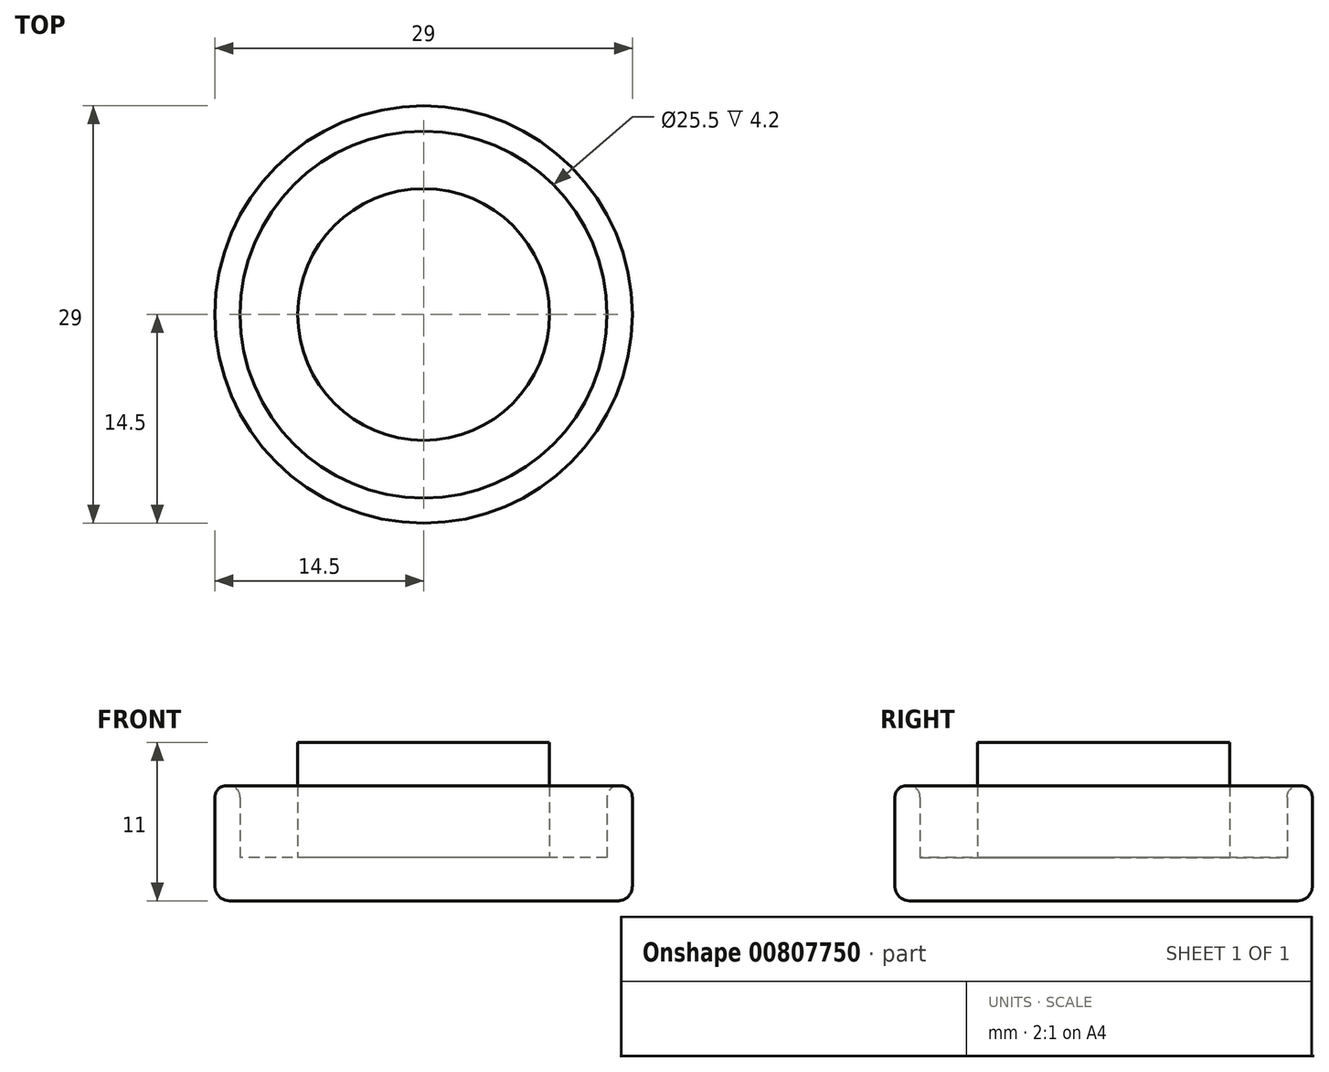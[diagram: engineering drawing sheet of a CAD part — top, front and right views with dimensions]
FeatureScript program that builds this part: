
annotation { "Feature Type Name" : "Feature", "Feature Type Description" : "" }
export const myFeature = defineFeature(function(context is Context, id is Id, definition is map)
    precondition{}
    {
        {
            var Q0;
            Q0=qCreatedBy(makeId("Top.planeOp"),FACE);
            var sketch = newSketch(context, id + "F0", { "sketchPlane" : qUnion([Q0])});
            skCircle(sketch, "E0", {"center": v(0, 0) * mm, "radius": 14.5 * mm});
            skSolve(sketch);
        }
        {
            var Q0;
            Q0=makeQuery(id+"F0.imprint","IMPRINT",FACE,{"disambiguationData":[TD([[makeQuery(id+"F0.imprint","IMPRINT",EDGE,{"derivedFrom":sQuery(id+"F0.wireOp",EDGE,"E0")}),1.0]])]});
            extrude(context, id + "F1", {"entities" : qUnion([Q0]), "depth" : 3 * mm, "offsetDistance" : 25 * mm});
        }
        {
            var Q0;
            Q0=makeQuery(id+"F1.opExtrude","CAP_FACE",FACE,{"disambiguationData":[OSD([sQuery(id+"F0.wireOp",EDGE,"E0")])],"isStart":false});
            var sketch = newSketch(context, id + "F2", { "sketchPlane" : qUnion([Q0])});
            skCircle(sketch, "E1", {"center": v(0, 0) * mm, "radius": 8.75 * mm});
            skSolve(sketch);
        }
        {
            var Q0;
            Q0=makeQuery(id+"F2.imprint","IMPRINT",FACE,{"disambiguationData":[TD([[makeQuery(id+"F2.imprint","IMPRINT",EDGE,{"derivedFrom":sQuery(id+"F2.wireOp",EDGE,"E1")}),1.0]])]});
            extrude(context, id + "F3", {"entities" : qUnion([Q0]), "operationType" : NewBodyOperationType.ADD, "depth" : 8 * mm, "offsetDistance" : 25 * mm});
        }
        {
            var Q0;
            Q0=makeQuery(id+"F1.opExtrude","CAP_EDGE",EDGE,{"disambiguationData":[OSD([sQuery(id+"F0.wireOp",EDGE,"E0")])],"isStart":true});
            fillet(context, id + "F4", {"entities" : qUnion([Q0]), "radius" : 1 * mm, "tangentPropagation" : true, "allowEdgeOverflow" : false});
        }
        {
            var Q0;
            Q0=makeQuery(id+"F1.opExtrude","CAP_FACE",FACE,{"disambiguationData":[OSD([sQuery(id+"F0.wireOp",EDGE,"E0")])],"isStart":false});
            var sketch = newSketch(context, id + "F5", { "sketchPlane" : qUnion([Q0])});
            skCircle(sketch, "E2", {"center": v(0, 0) * mm, "radius": 12.75 * mm});
            skSolve(sketch);
        }
        {
            var Q0;
            Q0=makeQuery(id+"F5.imprint","IMPRINT",FACE,{"disambiguationData":[TD([[makeQuery(id+"F5.imprint","IMPRINT",EDGE,{"derivedFrom":sQuery(id+"F5.wireOp",EDGE,"E2")}),-1.0]])]});
            extrude(context, id + "F6", {"entities" : qUnion([Q0]), "operationType" : NewBodyOperationType.ADD, "depth" : 5 * mm, "offsetDistance" : 25 * mm});
        }
        {
            var Q0;
            Q0=makeQuery(id+"F6.opExtrude","CAP_EDGE",EDGE,{"disambiguationData":[OSD([sQuery(id+"F0.wireOp",EDGE,"E0")])],"isStart":false});
            var Q1;
            Q1=makeQuery(id+"F6.opExtrude","CAP_EDGE",EDGE,{"disambiguationData":[OSD([sQuery(id+"F5.wireOp",EDGE,"E2")])],"isStart":false});
            fillet(context, id + "F7", {"entities" : qUnion([Q0, Q1]), "radius" : .8 * mm, "tangentPropagation" : true, "allowEdgeOverflow" : false});
        }
    });
